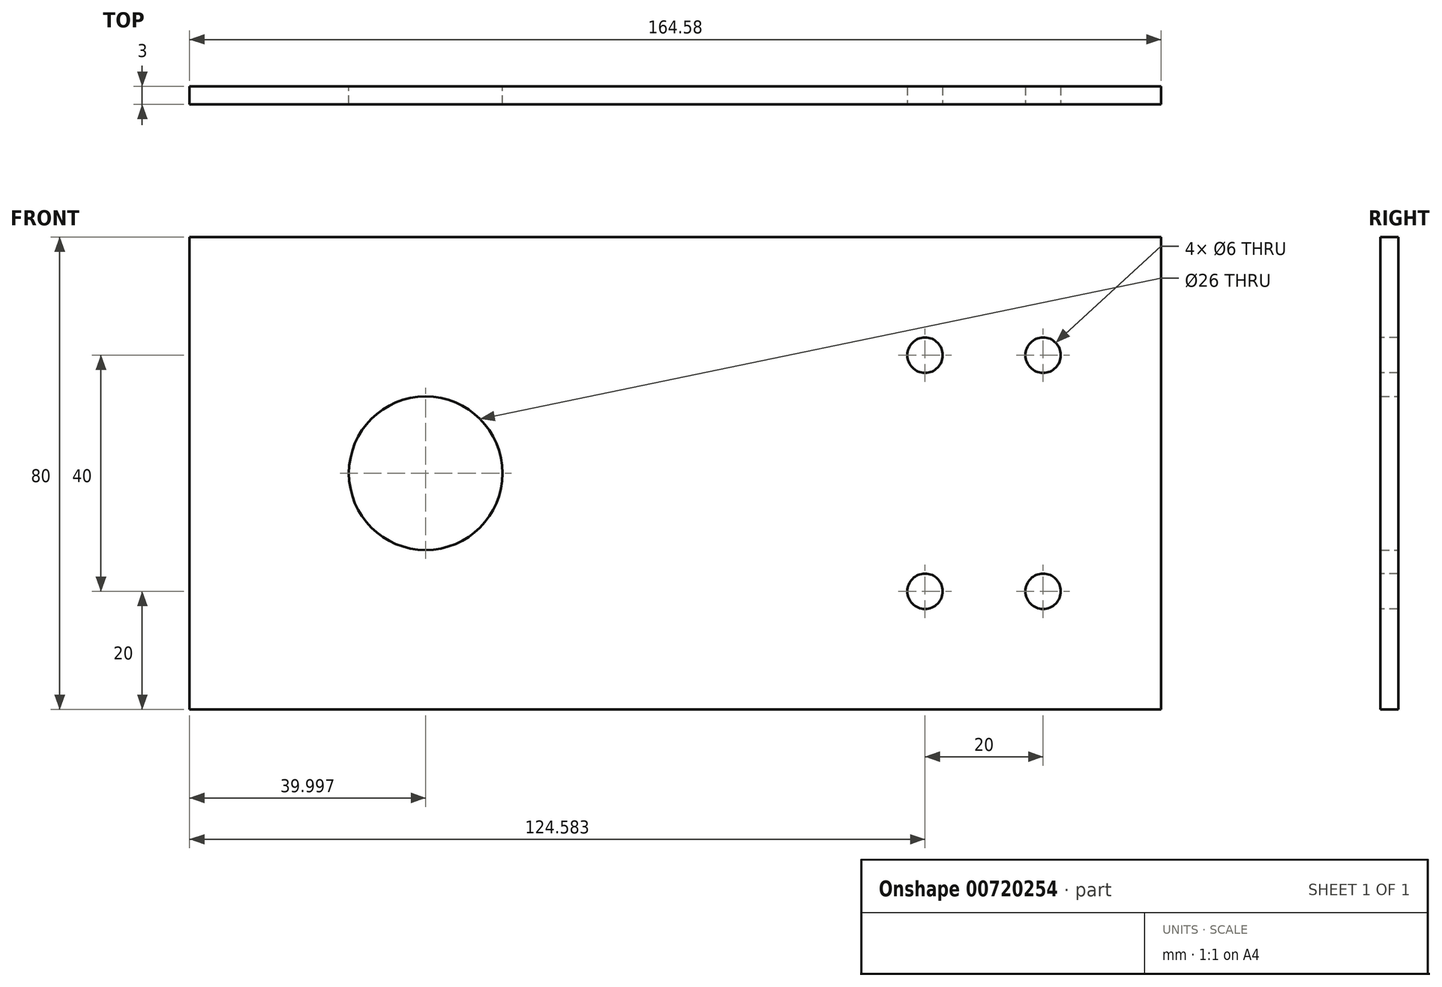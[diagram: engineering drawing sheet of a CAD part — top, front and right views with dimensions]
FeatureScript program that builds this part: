
annotation { "Feature Type Name" : "Feature", "Feature Type Description" : "" }
export const myFeature = defineFeature(function(context is Context, id is Id, definition is map)
    precondition{}
    {
        {
            var Q0;
            Q0=qCreatedBy(makeId("Front.planeOp"),FACE);
            var sketch = newSketch(context, id + "F0", { "sketchPlane" : qUnion([Q0])});
            skLineSegment(sketch, "E0.bottom", {"start": v(82.3, 40) * mm, "end": v(-82.3, 40) * mm});
            skLineSegment(sketch, "E0.top", {"start": v(82.3, -40) * mm, "end": v(-82.3, -40) * mm});
            skLineSegment(sketch, "E0.left", {"start": v(82.3, 40) * mm, "end": v(82.3, -40) * mm});
            skLineSegment(sketch, "E0.right", {"start": v(-82.3, 40) * mm, "end": v(-82.3, -40) * mm});
            skPoint(sketch, "E0.middle", {"position": v(0, 0) * mm});
            skLineSegment(sketch, "E1", {"start": v(-82.3, 20) * mm, "end": v(82.3, 20) * mm, "construction": true});
            skLineSegment(sketch, "E2", {"start": v(-82.3, -20) * mm, "end": v(82.3, -20) * mm, "construction": true});
            skCircle(sketch, "E3", {"center": v(-42.3, 0) * mm, "radius": 13 * mm});
            skCircle(sketch, "E4", {"center": v(-42.3, 0) * mm, "radius": 40 * mm, "construction": true});
            skPoint(sketch, "E5", {"position": v(62.3, 20) * mm});
            skPoint(sketch, "E6", {"position": v(42.3, 20) * mm});
            skPoint(sketch, "E7", {"position": v(42.3, -20) * mm});
            skPoint(sketch, "E8", {"position": v(62.3, -20) * mm});
            skSolve(sketch);
        }
        {
            var Q0;
            Q0=makeQuery(id+"F0.imprint","IMPRINT",FACE,{"disambiguationData":[TD([[makeQuery(id+"F0.imprint","IMPRINT",EDGE,{"derivedFrom":sQuery(id+"F0.wireOp",EDGE,"E0.bottom")}),1.0]])]});
            extrude(context, id + "F1", {"entities" : qUnion([Q0]), "depth" : 3 * mm, "offsetDistance" : 25 * mm});
        }
        {
            var Q0;
            Q0=sQuery(id+"F0.wireOp",VERTEX,"E6");
            var Q1;
            Q1=sQuery(id+"F0.wireOp",VERTEX,"E5");
            var Q2;
            Q2=sQuery(id+"F0.wireOp",VERTEX,"E8");
            var Q3;
            Q3=sQuery(id+"F0.wireOp",VERTEX,"E7");
            var Q4;
            Q4=makeQuery(id+"F1.opExtrude","SWEPT_BODY",BODY,{"disambiguationData":[OSD([sQuery(id+"F0.wireOp",EDGE,"E0.bottom"),sQuery(id+"F0.wireOp",EDGE,"E0.top"),sQuery(id+"F0.wireOp",EDGE,"E0.left"),sQuery(id+"F0.wireOp",EDGE,"E0.right"),sQuery(id+"F0.wireOp",EDGE,"E3")])]});
            hole(context, id + "F2", {"style" : HoleStyle.SIMPLE, "endStyle" : HoleEndStyle.BLIND, "oppositeDirection" : true, "holeDiameter" : 6 * mm, "majorDiameter" : 5 * mm, "holeDepth" : 40 * mm, "tappedDepth" : 12 * mm, "tapClearance" : 3, "locations" : qUnion([Q0, Q1, Q2, Q3]), "scope" : qUnion([Q4])});
        }
    });
